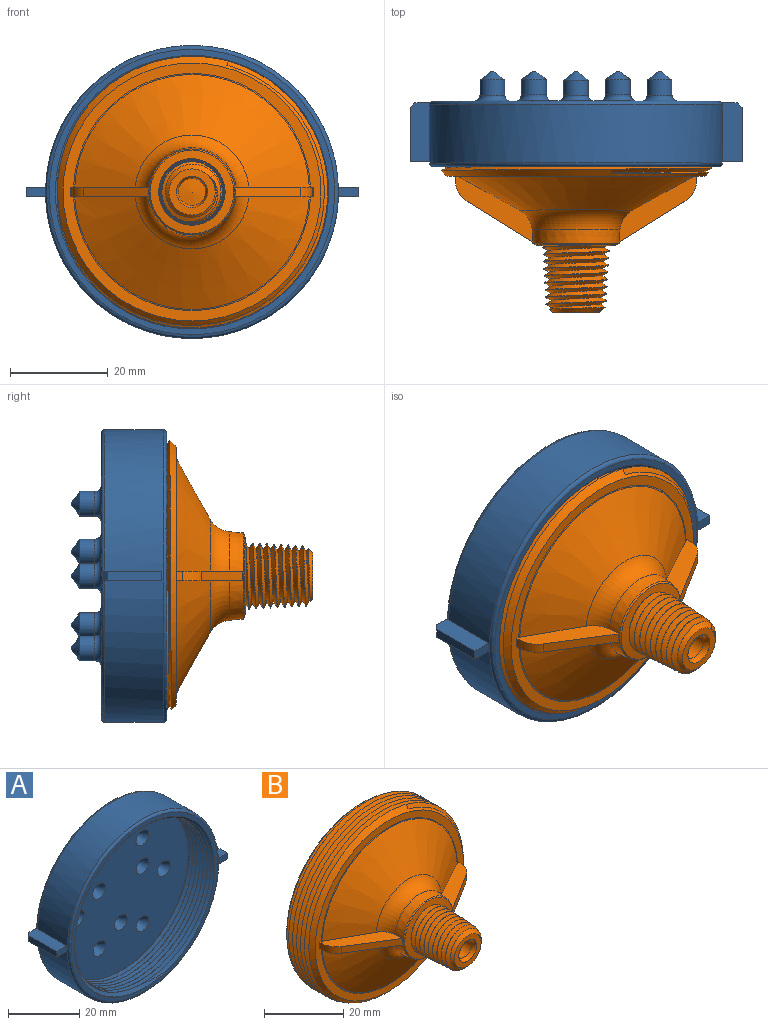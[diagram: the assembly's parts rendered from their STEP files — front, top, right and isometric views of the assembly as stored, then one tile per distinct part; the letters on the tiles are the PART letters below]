
ASSEMBLY  parts=2 mates=1
PART A: 79 faces, bbox 68x20.5x64.9 mm
  f0: cylinder r=26.8mm len=53.59mm, axis (0,-1,0), area 48.2mm2, adj f2,f52,f53,f54,f78
  f1: plane 58.43x58.43mm, normal (0,-1,0), area 222.5mm2, adj f51,f52,f53,f58,f78
  f2: plane 53.59x53.59mm, normal (0,-1,0), area 2073.5mm2, adj f0,f24,f26,f28,f30,f32,f34,f36
  f3: plane 58.42x58.42mm, normal (0,1,0), area 2270mm2, adj f59,f60,f61,f62,f63,f64,f65,f66
  f4: cylinder r=29.97mm len=59.94mm, axis (0,-1,0), area 2194.7mm2, adj f41,f42,f43,f46,f47,f50,f58,f59
  f5: cylinder r=2.54mm len=5.08mm, axis (0,-1,0), area 49.2mm2, adj f68,f75
  f6: plane 0.61x0.61mm, normal (0,1,0), area 0.1mm2, adj f31,f75
  f7: cylinder r=2.54mm len=5.08mm, axis (0,-1,0), area 49.2mm2, adj f67,f77
  f8: plane 0.61x0.61mm, normal (0,1,0), area 0.1mm2, adj f33,f77
  f9: cylinder r=2.54mm len=5.08mm, axis (0,-1,0), area 49.2mm2, adj f66,f76
  f10: plane 0.61x0.61mm, normal (0,1,0), area 0.1mm2, adj f29,f76
  f11: cylinder r=2.54mm len=5.08mm, axis (0,-1,0), area 49.2mm2, adj f65,f69
  f12: plane 0.61x0.61mm, normal (0,1,0), area 0.1mm2, adj f37,f69
  f13: cylinder r=2.54mm len=5.08mm, axis (0,-1,0), area 49.2mm2, adj f64,f70
  f14: plane 0.61x0.61mm, normal (0,1,0), area 0.1mm2, adj f35,f70
  f15: cylinder r=2.54mm len=5.08mm, axis (0,-1,0), area 49.2mm2, adj f63,f71
  f16: plane 0.61x0.61mm, normal (0,1,0), area 0.1mm2, adj f39,f71
  f17: cylinder r=2.54mm len=5.08mm, axis (0,-1,0), area 49.2mm2, adj f62,f72
  f18: plane 0.61x0.61mm, normal (0,1,0), area 0.1mm2, adj f27,f72
  f19: cylinder r=2.54mm len=5.08mm, axis (0,-1,0), area 49.2mm2, adj f61,f73
  f20: plane 0.61x0.61mm, normal (0,1,0), area 0.1mm2, adj f25,f73
  f21: cylinder r=2.54mm len=5.08mm, axis (0,-1,0), area 49.2mm2, adj f60,f74
  f22: plane 0.61x0.61mm, normal (0,1,0), area 0.1mm2, adj f23,f74
  f23: cylinder r=0.23mm len=7.15mm, axis (0,-1,0), area 10.3mm2, adj f22,f24
  f24: cone r=0.23mm half-angle=37.5deg, axis (0,-1,0), area 33mm2, adj f2,f23
  f25: cylinder r=0.23mm len=7.15mm, axis (0,-1,0), area 10.3mm2, adj f20,f26
  f26: cone r=0.23mm half-angle=37.5deg, axis (0,-1,0), area 33mm2, adj f2,f25
  f27: cylinder r=0.23mm len=7.15mm, axis (0,-1,0), area 10.3mm2, adj f18,f28
  f28: cone r=0.23mm half-angle=37.5deg, axis (0,-1,0), area 33mm2, adj f2,f27
  f29: cylinder r=0.23mm len=7.15mm, axis (0,-1,0), area 10.3mm2, adj f10,f30
  f30: cone r=0.23mm half-angle=37.5deg, axis (0,-1,0), area 33mm2, adj f2,f29
  f31: cylinder r=0.23mm len=7.15mm, axis (0,-1,0), area 10.3mm2, adj f6,f32
  f32: cone r=0.23mm half-angle=37.5deg, axis (0,-1,0), area 33mm2, adj f2,f31
  f33: cylinder r=0.23mm len=7.15mm, axis (0,-1,0), area 10.3mm2, adj f8,f34
  f34: cone r=0.23mm half-angle=37.5deg, axis (0,-1,0), area 33mm2, adj f2,f33
  f35: cylinder r=0.23mm len=7.15mm, axis (0,-1,0), area 10.3mm2, adj f14,f36
  f36: cone r=0.23mm half-angle=37.5deg, axis (0,-1,0), area 33mm2, adj f2,f35
  f37: cylinder r=0.23mm len=7.15mm, axis (0,-1,0), area 10.3mm2, adj f12,f38
  f38: cone r=0.23mm half-angle=37.5deg, axis (0,-1,0), area 33mm2, adj f2,f37
  f39: cylinder r=0.23mm len=7.15mm, axis (0,-1,0), area 10.3mm2, adj f16,f40
  f40: cone r=0.23mm half-angle=37.5deg, axis (0,-1,0), area 33mm2, adj f2,f39
  f41: plane 12.11x4.17mm, normal (0,0,1), area 48.1mm2, adj f4,f43,f44,f45,f56,f59
  f42: plane 12.11x4.17mm, normal (0,0,-1), area 48.1mm2, adj f4,f43,f44,f45,f56,f59
  f43: plane 4.01x2.03mm, normal (0,-1,0), area 8.1mm2, adj f4,f41,f42,f44
  f44: plane 11.09x2.03mm, normal (1,0,0), area 22.5mm2, adj f41,f42,f43,f56
  f45: plane 3.15x2.03mm, normal (0,1,0), area 6.4mm2, adj f41,f42,f56,f59
  f46: plane 12.11x4.17mm, normal (0,0,1), area 48.1mm2, adj f4,f48,f49,f50,f57,f59
  f47: plane 12.11x4.17mm, normal (0,0,-1), area 48.1mm2, adj f4,f48,f49,f50,f57,f59
  f48: plane 3.15x2.03mm, normal (0,1,0), area 6.4mm2, adj f46,f47,f57,f59
  f49: plane 11.09x2.03mm, normal (-1,0,0), area 22.5mm2, adj f46,f47,f50,f57
  f50: plane 4.01x2.03mm, normal (0,-1,0), area 8.1mm2, adj f4,f46,f47,f49
  f51: plane 0.16x0.1mm, normal (-0.95,0,-0.3), area 0mm2, adj f1,f52,f78
  f52: bspline ~64.71x56.04mm, area 1595.6mm2, adj f0,f1,f51,f53,f54,f55,f78
  f53: bspline ~64.71x56.04mm, area 1467.2mm2, adj f0,f1,f52,f54,f78
  f54: plane 1.41x1.22mm, normal (-1,0,0), area 0.9mm2, adj f0,f52,f53,f55
  f55: cylinder r=26.8mm len=53.34mm, axis (0,-1,0), area 27.7mm2, adj f2,f52,f54
  f56: plane 2.03x1.02mm, normal (0.71,0.71,0), area 2.9mm2, adj f41,f42,f44,f45
  f57: plane 2.03x1.02mm, normal (-0.71,0.71,0), area 2.9mm2, adj f46,f47,f48,f49
  f58: torus R=29.21mm, axis (0,1,0), area 223.3mm2, adj f1,f4
  f59: torus R=29.21mm, axis (0,-1,0), area 221.4mm2, adj f3,f4,f41,f42,f45,f46,f47,f48
  f60: torus R=3.81mm, axis (0,-1,0), area 37.6mm2, adj f3,f21
  f61: torus R=3.81mm, axis (0,-1,0), area 37.6mm2, adj f3,f19
  f62: torus R=3.81mm, axis (0,-1,0), area 37.6mm2, adj f3,f17
  f63: torus R=3.81mm, axis (0,-1,0), area 37.6mm2, adj f3,f15
  f64: torus R=3.81mm, axis (0,-1,0), area 37.6mm2, adj f3,f13
  f65: torus R=3.81mm, axis (0,-1,0), area 37.6mm2, adj f3,f11
  f66: torus R=3.81mm, axis (0,-1,0), area 37.6mm2, adj f3,f9
  f67: torus R=3.81mm, axis (0,-1,0), area 37.6mm2, adj f3,f7
  f68: torus R=3.81mm, axis (0,-1,0), area 37.6mm2, adj f3,f5
  f69: cone r=2.54mm half-angle=51.5deg, axis (0,-1,0), area 25.5mm2, adj f11,f12
  f70: cone r=2.54mm half-angle=51.5deg, axis (0,-1,0), area 25.5mm2, adj f13,f14
  f71: cone r=2.54mm half-angle=51.5deg, axis (0,-1,0), area 25.5mm2, adj f15,f16
  f72: cone r=2.54mm half-angle=51.5deg, axis (0,-1,0), area 25.5mm2, adj f17,f18
  f73: cone r=2.54mm half-angle=51.5deg, axis (0,-1,0), area 25.5mm2, adj f19,f20
  f74: cone r=2.54mm half-angle=51.5deg, axis (0,-1,0), area 25.5mm2, adj f21,f22
  f75: cone r=2.54mm half-angle=51.5deg, axis (0,-1,0), area 25.5mm2, adj f5,f6
  f76: cone r=2.54mm half-angle=51.5deg, axis (0,-1,0), area 25.5mm2, adj f9,f10
  f77: cone r=2.54mm half-angle=51.5deg, axis (0,-1,0), area 25.5mm2, adj f7,f8
  f78: cone r=26.8mm half-angle=57deg, axis (0,-1,0), area 118.5mm2, adj f0,f1,f51,f52,f53
PART B: 45 faces, bbox 55.9x42.1x64.5 mm
  f0: plane 52.78x52.78mm, normal (0,1,0), area 160.5mm2, adj f1,f18
  f1: bspline ~50.81x50.81mm, area 707.1mm2, adj f0,f2
  f2: plane 44.89x44.89mm, normal (0,1,0), area 237.3mm2, adj f1,f3
  f3: plane 41.32x41.32mm, normal (0,1,0), area 48.1mm2, adj f2,f4
  f4: cylinder r=20.28mm len=40.56mm, axis (0,-1,0), area 1116.2mm2, adj f3,f5
  f5: plane 40.76x40.76mm, normal (0,-1,0), area 12.4mm2, adj f4,f6
  f6: cone r=22.65mm half-angle=61deg, axis (0,1,0), area 1421.5mm2, adj f5,f7
  f7: torus R=5.31mm, axis (0,1,0), area 64.8mm2, adj f6,f8
  f8: cylinder r=2.77mm len=16.71mm, axis (0,-1,0), area 290.4mm2, adj f7,f9
  f9: torus R=5.31mm, axis (0,-1,0), area 26.7mm2, adj f8,f10
  f10: cylinder r=3.17mm len=6.35mm, axis (0,-1,0), area 0.5mm2, adj f9,f11
  f11: plane 9.44x9.44mm, normal (0,-1,0), area 38.3mm2, adj f10,f12
  f12: cone r=4.72mm half-angle=46.5deg, axis (0,1,0), area 28.8mm2, adj f11,f13,f17
  f13: bspline ~15.33x13.77mm, area 453mm2, adj f12,f14,f15,f16,f17
  f14: cone r=8.79mm half-angle=84.6deg, axis (0,1,0), area 123.5mm2, adj f13,f15,f16
  f15: bspline ~14.35x13.9mm, area 448.1mm2, adj f13,f14,f16,f17
  f16: cone r=6.13mm half-angle=3.1deg, axis (0,1,0), area 26.4mm2, adj f13,f14,f15,f17
  f17: cone r=4.72mm half-angle=46.5deg, axis (0,1,0), area 9.6mm2, adj f12,f13,f15,f16
  f18: cone r=27.81mm half-angle=45deg, axis (0,-1,0), area 171.7mm2, adj f0,f19,f20,f44
  f19: cone r=27.81mm half-angle=45deg, axis (0,-1,0), area 19.5mm2, adj f18,f20,f44
  f20: bspline ~55.5x55.43mm, area 1449.2mm2, adj f18,f19,f21,f43,f44
  f21: cone r=26.39mm half-angle=45deg, axis (0,1,0), area 231.3mm2, adj f20,f22,f43
  f22: plane 52.78x52.78mm, normal (0,-1,0), area 336.7mm2, adj f21,f23,f36,f37,f38,f39,f40,f41
  f23: torus R=24.26mm, axis (0,-1,0), area 19mm2, adj f22,f24,f36,f42
  f24: cone r=24.13mm half-angle=61deg, axis (0,1,0), area 760.6mm2, adj f23,f25,f36,f42
  f25: torus R=14.11mm, axis (0,-1,0), area 146.5mm2, adj f24,f26,f35,f36,f42
  f26: cone r=9.31mm half-angle=4.9deg, axis (0,1,0), area 148mm2, adj f25,f27,f29,f31,f33,f35,f36,f38
  f27: plane 13.6x8.54mm, normal (0.53,-0.85,0), area 32.3mm2, adj f26,f28,f40,f42
  f28: cylinder r=5.08mm len=3.87mm, axis (0,0,-1), area 9.6mm2, adj f27,f40,f41,f42
  f29: torus R=14.11mm, axis (0,-1,0), area 146.7mm2, adj f26,f30,f38,f40
  f30: cone r=24.13mm half-angle=61deg, axis (0,1,0), area 760.6mm2, adj f29,f38,f39,f40
  f31: plane 13.6x8.54mm, normal (-0.53,-0.85,0), area 32.3mm2, adj f26,f32,f36,f38
  f32: cylinder r=5.08mm len=3.87mm, axis (0,0,-1), area 9.6mm2, adj f31,f36,f37,f38
  f33: cone r=8.54mm half-angle=44.7deg, axis (0,1,0), area 21.3mm2, adj f26,f34
  f34: cone r=8.79mm half-angle=84.6deg, axis (0,1,0), area 230mm2, adj f33
  f35: cone r=9.31mm half-angle=4.9deg, axis (0,1,0), area 0mm2, adj f25,f26,f42
  f36: plane 16.28x13.88mm, normal (0,0,1), area 68.5mm2, adj f22,f23,f24,f25,f26,f31,f32,f37
  f37: plane 2.03x1.27mm, normal (-1,-0.09,0), area 2.6mm2, adj f22,f32,f36,f38
  f38: plane 16.28x13.88mm, normal (0,0,-1), area 68.5mm2, adj f22,f26,f29,f30,f31,f32,f37,f39
  f39: torus R=24.26mm, axis (0,-1,0), area 19mm2, adj f22,f30,f38,f40
  f40: plane 16.28x13.88mm, normal (0,0,-1), area 68.5mm2, adj f22,f26,f27,f28,f29,f30,f39,f41
  f41: plane 2.03x1.27mm, normal (1,-0.09,0), area 2.6mm2, adj f22,f28,f40,f42
  f42: plane 16.28x13.88mm, normal (0,0,1), area 68.5mm2, adj f22,f23,f24,f25,f27,f28,f35,f41
  f43: plane 1.18x0.9mm, normal (0.96,0,-0.27), area 0.2mm2, adj f20,f21,f44
  f44: bspline ~64.21x55.6mm, area 1432.2mm2, adj f18,f19,f20,f43
PLACE A t=(0,43.3,0)mm
PLACE B t=(0,38.1,0)mm
MATE slider B.f4 <-> A.f0  axis (0,1,0) through (0,29.35,0)mm
